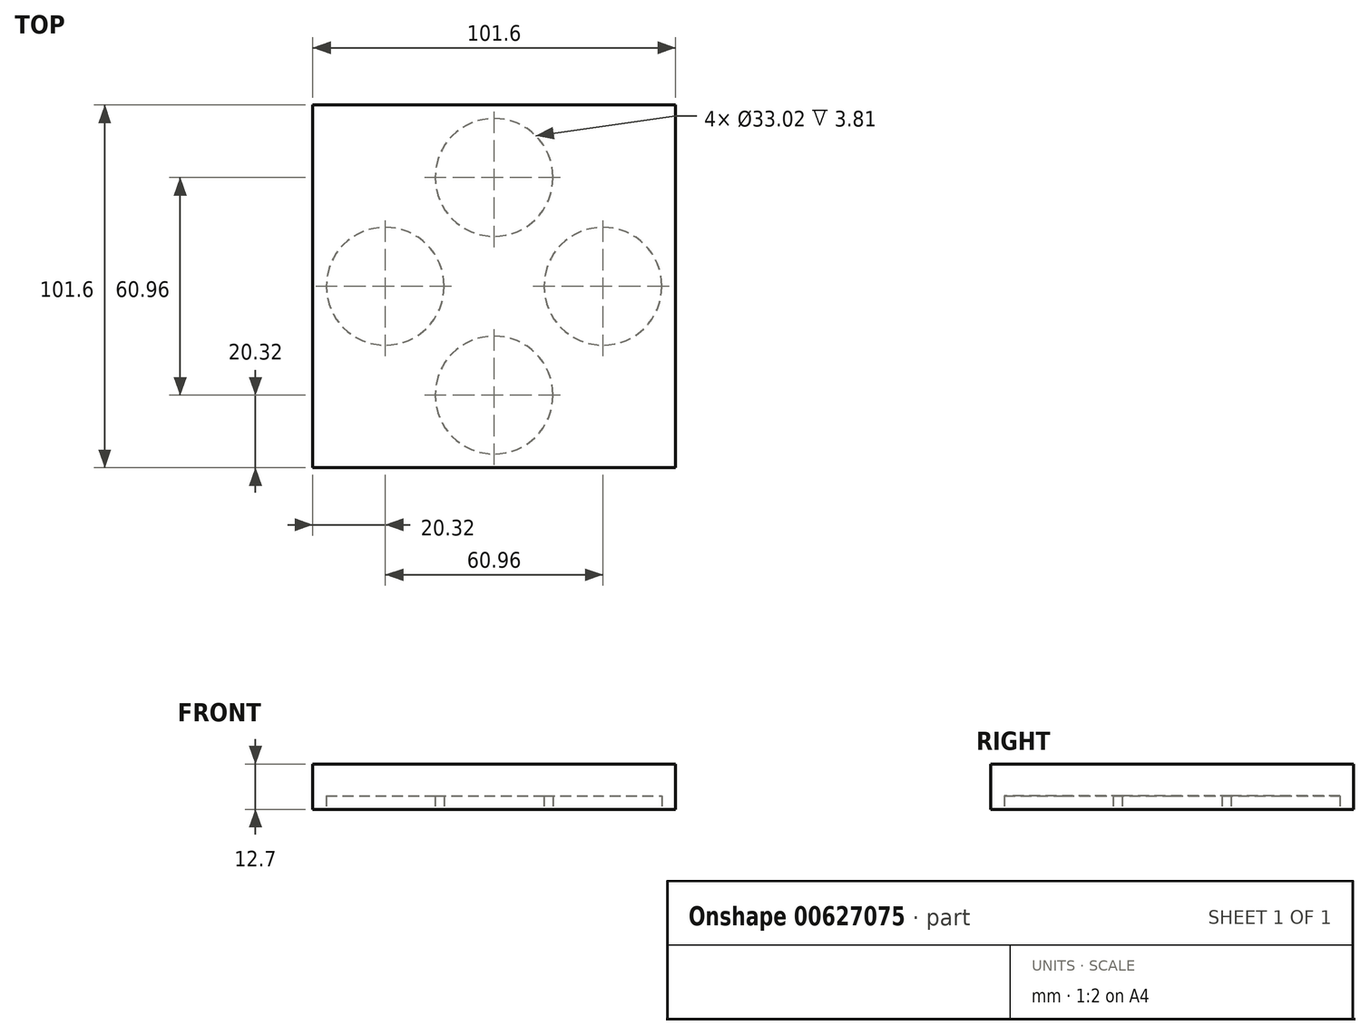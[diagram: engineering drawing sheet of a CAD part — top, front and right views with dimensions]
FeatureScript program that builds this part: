
annotation { "Feature Type Name" : "Feature", "Feature Type Description" : "" }
export const myFeature = defineFeature(function(context is Context, id is Id, definition is map)
    precondition{}
    {
        {
            var Q0;
            Q0=qCreatedBy(makeId("Top.planeOp"),FACE);
            var sketch = newSketch(context, id + "F0", { "sketchPlane" : qUnion([Q0])});
            skLineSegment(sketch, "E0.bottom", {"start": v(50.8, 50.8) * mm, "end": v(-50.8, 50.8) * mm});
            skLineSegment(sketch, "E0.top", {"start": v(50.8, -50.8) * mm, "end": v(-50.8, -50.8) * mm});
            skLineSegment(sketch, "E0.left", {"start": v(50.8, 50.8) * mm, "end": v(50.8, -50.8) * mm});
            skLineSegment(sketch, "E0.right", {"start": v(-50.8, 50.8) * mm, "end": v(-50.8, -50.8) * mm});
            skPoint(sketch, "E0.middle", {"position": v(0, 0) * mm});
            skSolve(sketch);
        }
        {
            var Q0;
            Q0=makeQuery(id+"F0.imprint","IMPRINT",FACE,{"disambiguationData":[TD([[makeQuery(id+"F0.imprint","IMPRINT",EDGE,{"derivedFrom":sQuery(id+"F0.wireOp",EDGE,"E0.bottom")}),1.0]])]});
            extrude(context, id + "F1", {"entities" : qUnion([Q0]), "depth" : 12.7 * mm, "offsetDistance" : 25.4 * mm});
        }
        {
            var Q0;
            Q0=makeQuery(id+"F1.opExtrude","CAP_FACE",FACE,{"disambiguationData":[OSD([sQuery(id+"F0.wireOp",EDGE,"E0.bottom"),sQuery(id+"F0.wireOp",EDGE,"E0.top"),sQuery(id+"F0.wireOp",EDGE,"E0.left"),sQuery(id+"F0.wireOp",EDGE,"E0.right")])],"isStart":true});
            var sketch = newSketch(context, id + "F2", { "sketchPlane" : qUnion([Q0])});
            skCircle(sketch, "E1", {"center": v(0, 30.48) * mm, "radius": 16.51 * mm});
            skCircle(sketch, "E2", {"center": v(-30.48, 0) * mm, "radius": 16.51 * mm});
            skCircle(sketch, "E3", {"center": v(30.48, 0) * mm, "radius": 16.51 * mm});
            skCircle(sketch, "E4", {"center": v(0, -30.48) * mm, "radius": 16.51 * mm});
            skSolve(sketch);
        }
        {
            var Q0;
            Q0=makeQuery(id+"F2.imprint","IMPRINT",FACE,{"disambiguationData":[TD([[makeQuery(id+"F2.imprint","IMPRINT",EDGE,{"derivedFrom":sQuery(id+"F2.wireOp",EDGE,"E2")}),1.0]])]});
            var Q1;
            Q1=makeQuery(id+"F2.imprint","IMPRINT",FACE,{"disambiguationData":[TD([[makeQuery(id+"F2.imprint","IMPRINT",EDGE,{"derivedFrom":sQuery(id+"F2.wireOp",EDGE,"E1")}),1.0]])]});
            var Q2;
            Q2=makeQuery(id+"F2.imprint","IMPRINT",FACE,{"disambiguationData":[TD([[makeQuery(id+"F2.imprint","IMPRINT",EDGE,{"derivedFrom":sQuery(id+"F2.wireOp",EDGE,"E3")}),1.0]])]});
            var Q3;
            Q3=makeQuery(id+"F2.imprint","IMPRINT",FACE,{"disambiguationData":[TD([[makeQuery(id+"F2.imprint","IMPRINT",EDGE,{"derivedFrom":sQuery(id+"F2.wireOp",EDGE,"E4")}),1.0]])]});
            extrude(context, id + "F3", {"entities" : qUnion([Q0, Q1, Q2, Q3]), "operationType" : NewBodyOperationType.REMOVE, "oppositeDirection" : true, "depth" : 3.8 * mm, "offsetDistance" : 25.4 * mm});
        }
    });
